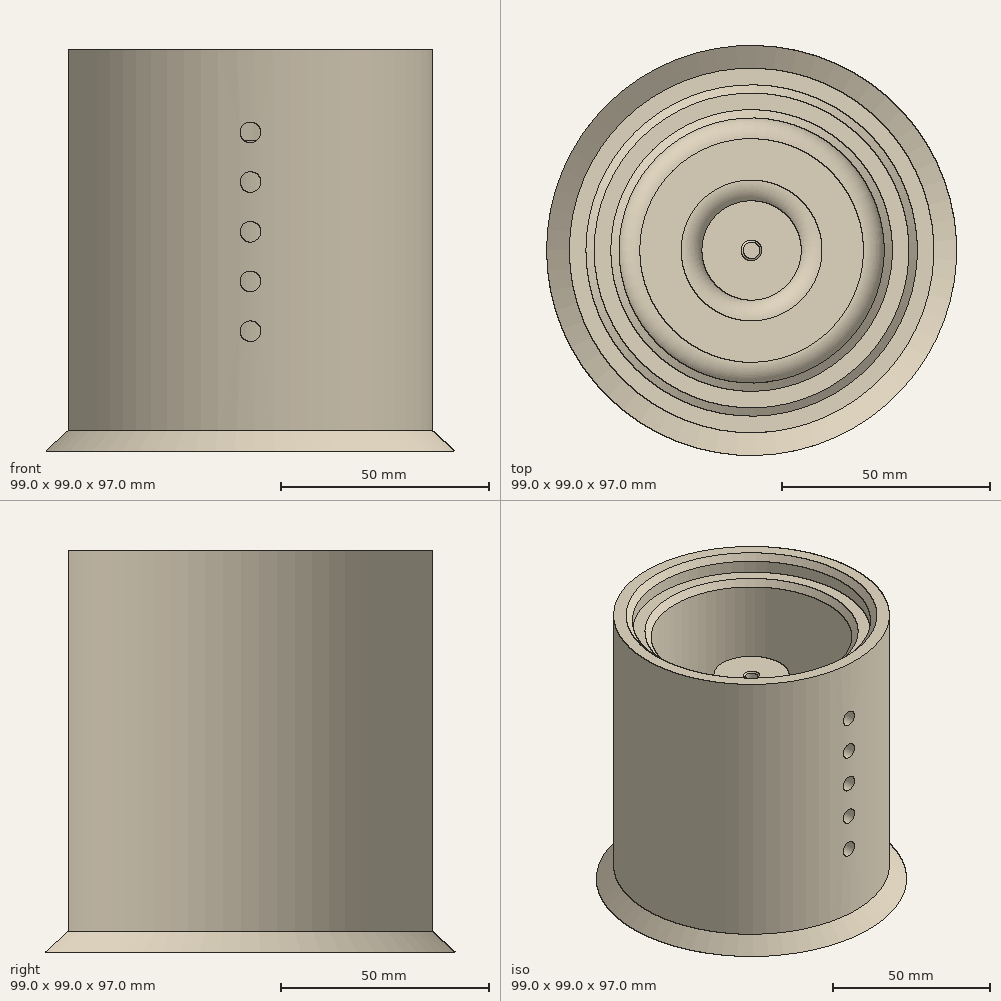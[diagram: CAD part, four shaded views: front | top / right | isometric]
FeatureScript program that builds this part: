
annotation { "Feature Type Name" : "Feature", "Feature Type Description" : "" }
export const myFeature = defineFeature(function(context is Context, id is Id, definition is map)
    precondition{}
    {
        {
            var Q0;
            Q0=qCreatedBy(makeId("Front.planeOp"),FACE);
            var sketch = newSketch(context, id + "F0", { "sketchPlane" : qUnion([Q0])});
            skLineSegment(sketch, "E0", {"start": v(0, 0) * mm, "end": v(0, 30) * mm});
            skLineSegment(sketch, "E1", {"start": v(0, 30) * mm, "end": v(2, 30) * mm});
            skLineSegment(sketch, "E2", {"start": v(2, 30) * mm, "end": v(2, 70) * mm});
            skLineSegment(sketch, "E3", {"start": v(2, 70) * mm, "end": v(12, 70) * mm});
            skLineSegment(sketch, "E4", {"start": v(12, 70) * mm, "end": v(12, 12) * mm});
            skLineSegment(sketch, "E5", {"start": v(12, 12) * mm, "end": v(32, 12) * mm});
            skLineSegment(sketch, "E6", {"start": v(32, 12) * mm, "end": v(32, 86) * mm});
            skLineSegment(sketch, "E7", {"start": v(32, 86) * mm, "end": v(38, 86) * mm});
            skLineSegment(sketch, "E8", {"start": v(38, 86) * mm, "end": v(38, 92) * mm});
            skLineSegment(sketch, "E9", {"start": v(38, 92) * mm, "end": v(44, 92) * mm});
            skLineSegment(sketch, "E10", {"start": v(44, 92) * mm, "end": v(44, 0) * mm});
            skLineSegment(sketch, "E11", {"start": v(44, 0) * mm, "end": v(49.5, -5) * mm});
            skLineSegment(sketch, "E12", {"start": v(49.5, -5) * mm, "end": v(32, -5) * mm});
            skLineSegment(sketch, "E13", {"start": v(32, -5) * mm, "end": v(32, 0) * mm});
            skLineSegment(sketch, "E14", {"start": v(32, 0) * mm, "end": v(0, 0) * mm});
            skSolve(sketch);
        }
        {
            var Q0;
            Q0 = qSketchRegion(id + "F0", true);
            var Q1;
            Q1=sQuery(id+"F0.wireOp",EDGE,"E0");
            revolve(context, id + "F1", {"entities" : qUnion([Q0]), "axis" : qUnion([Q1]), "revolveType" : RevolveType.FULL});
        }
        {
            var Q0;
            Q0=makeQuery(id+"F1.opRevolve","SWEPT_EDGE",EDGE,{"disambiguationData":[OSD([sQuery(id+"F0.wireOp",EDGE,"E6"),sQuery(id+"F0.wireOp",EDGE,"E7")])]});
            var Q1;
            Q1=makeQuery(id+"F1.opRevolve","SWEPT_EDGE",EDGE,{"disambiguationData":[OSD([sQuery(id+"F0.wireOp",EDGE,"E8"),sQuery(id+"F0.wireOp",EDGE,"E9")])]});
            chamfer(context, id + "F2", {"entities" : qUnion([Q0, Q1]), "width" : 2 * mm, "tangentPropagation" : true});
        }
        {
            var Q0;
            Q0=makeQuery(id+"F1.opRevolve","SWEPT_EDGE",EDGE,{"disambiguationData":[OSD([sQuery(id+"F0.wireOp",EDGE,"E4"),sQuery(id+"F0.wireOp",EDGE,"E5")])]});
            var Q1;
            Q1=makeQuery(id+"F1.opRevolve","SWEPT_EDGE",EDGE,{"disambiguationData":[OSD([sQuery(id+"F0.wireOp",EDGE,"E5"),sQuery(id+"F0.wireOp",EDGE,"E6")])]});
            fillet(context, id + "F3", {"entities" : qUnion([Q0, Q1]), "radius" : 5 * mm, "tangentPropagation" : true, "allowEdgeOverflow" : false});
        }
        {
            var Q0;
            Q0=makeQuery(id+"F1.opRevolve","SWEPT_EDGE",EDGE,{"disambiguationData":[OSD([sQuery(id+"F0.wireOp",EDGE,"E13"),sQuery(id+"F0.wireOp",EDGE,"E14")])]});
            fillet(context, id + "F4", {"entities" : qUnion([Q0]), "radius" : 5 * mm, "tangentPropagation" : true, "allowEdgeOverflow" : false});
        }
        {
            var Q0;
            Q0=makeQuery(id+"F1.opRevolve","SWEPT_EDGE",EDGE,{"disambiguationData":[OSD([sQuery(id+"F0.wireOp",EDGE,"E2"),sQuery(id+"F0.wireOp",EDGE,"E3")])]});
            chamfer(context, id + "F5", {"entities" : qUnion([Q0]), "width" : 0.5 * mm, "tangentPropagation" : true});
        }
        {
            var Q0;
            Q0=qCreatedBy(makeId("Front.planeOp"),FACE);
            cPlane(context, id + "F6", {"entities" : qUnion([Q0]), "cplaneType" : CPlaneType.OFFSET, "offset" : 44 * mm, "width" : 152.4 * mm, "height" : 152.4 * mm});
        }
        {
            var Q0;
            Q0=qCreatedBy(id+"F6.planeOp",FACE);
            var sketch = newSketch(context, id + "F7", { "sketchPlane" : qUnion([Q0])});
            skCircle(sketch, "E15", {"center": v(0, 24) * mm, "radius": 2.5 * mm});
            skCircle(sketch, "E16", {"center": v(0, 36) * mm, "radius": 2.5 * mm});
            skCircle(sketch, "E17", {"center": v(0, 48) * mm, "radius": 2.5 * mm});
            skCircle(sketch, "E18", {"center": v(0, 60) * mm, "radius": 2.5 * mm});
            skCircle(sketch, "E19", {"center": v(0, 72) * mm, "radius": 2.5 * mm});
            skSolve(sketch);
        }
        {
            var Q0;
            Q0 = qSketchRegion(id + "F7", true);
            extrude(context, id + "F8", {"entities" : qUnion([Q0]), "operationType" : NewBodyOperationType.REMOVE, "oppositeDirection" : true, "depth" : 14 * mm});
        }
        {
            var Q0;
            Q0=qCreatedBy(id+"F6.planeOp",FACE);
            var sketch = newSketch(context, id + "F9", { "sketchPlane" : qUnion([Q0])});
            skPoint(sketch, "E20", {"position": v(0, 72) * mm});
            skPoint(sketch, "E21", {"position": v(0, 59.45) * mm});
            skPoint(sketch, "E22", {"position": v(0, 47.58) * mm});
            skSolve(sketch);
        }
        {
            var Q0;
            Q0=sQuery(id+"F9.wireOp",VERTEX,"E20");
            var Q1;
            Q1=makeQuery(id+"F1.opRevolve","SWEPT_BODY",BODY,{"disambiguationData":[OSD([sQuery(id+"F0.wireOp",EDGE,"E0"),sQuery(id+"F0.wireOp",EDGE,"E1"),sQuery(id+"F0.wireOp",EDGE,"E2"),sQuery(id+"F0.wireOp",EDGE,"E3"),sQuery(id+"F0.wireOp",EDGE,"E4"),sQuery(id+"F0.wireOp",EDGE,"E5"),sQuery(id+"F0.wireOp",EDGE,"E6"),sQuery(id+"F0.wireOp",EDGE,"E7"),sQuery(id+"F0.wireOp",EDGE,"E8"),sQuery(id+"F0.wireOp",EDGE,"E9"),sQuery(id+"F0.wireOp",EDGE,"E10"),sQuery(id+"F0.wireOp",EDGE,"E11"),sQuery(id+"F0.wireOp",EDGE,"E12"),sQuery(id+"F0.wireOp",EDGE,"E13"),sQuery(id+"F0.wireOp",EDGE,"E14")])]});
            hole(context, id + "F10", {"style" : HoleStyle.SIMPLE, "endStyle" : HoleEndStyle.BLIND, "holeDiameter" : 5 * mm, "holeDepth" : 25.4 * mm, "isTappedThrough" : true, "tappedDepth" : 12.7 * mm, "tapClearance" : 3, "locations" : qUnion([Q0]), "scope" : qUnion([Q1])});
        }
    });
